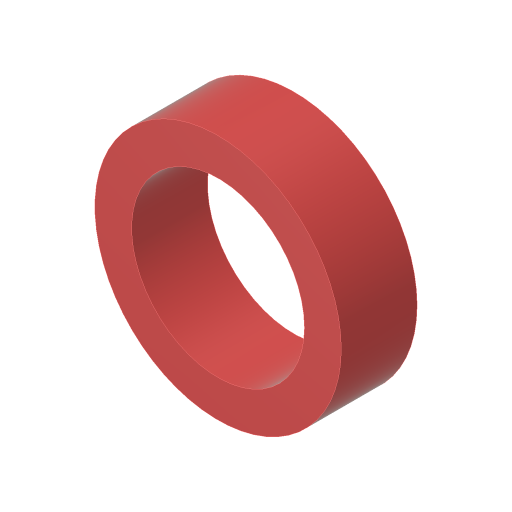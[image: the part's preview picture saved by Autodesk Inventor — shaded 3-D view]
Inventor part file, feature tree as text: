
AUTODESK INVENTOR PART (.ipt)
format: ipt  version: 2023.4 (Build 274418000, 418)  size: 114,176 bytes
history: native  units: in
note: dims shown in document units (in); Inventor stores cm internally (conversion verified against a paired STEP export)
features: extrude x1, sketch x1
ambient origin geometry x8: Origin, YZ Plane, XZ Plane, XY Plane, X Axis, Y Axis, Z Axis, Center Point
bodies: Solid1 (feature_tree)
feature tree (2):
  extrude  "Extrusion1"  Depth=0.257in
  sketch  "Sketch1"  dims[d0=0.585in d1=0.125in d2=0.257in d3=0.0in]
